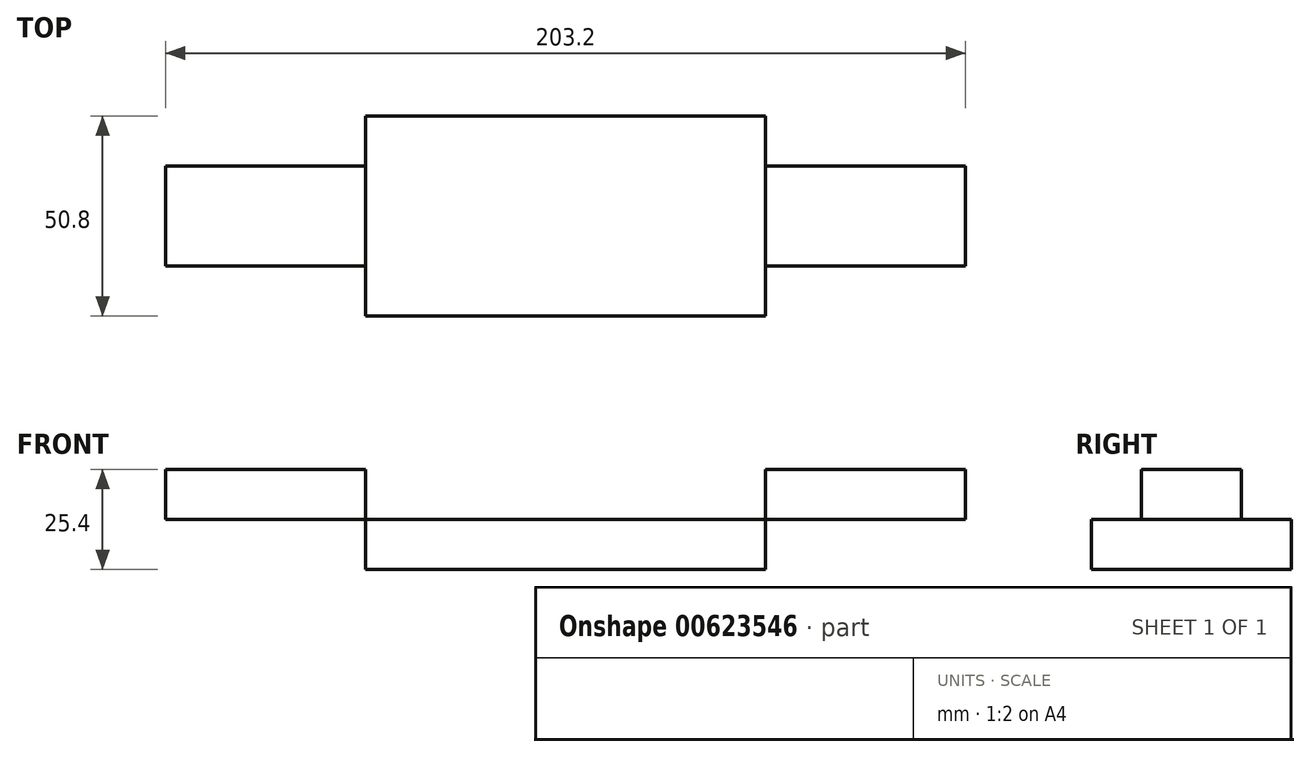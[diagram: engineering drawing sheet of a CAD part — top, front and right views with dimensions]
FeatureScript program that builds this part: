
annotation { "Feature Type Name" : "Feature", "Feature Type Description" : "" }
export const myFeature = defineFeature(function(context is Context, id is Id, definition is map)
    precondition{}
    {
        {
            var Q0;
            Q0=qCreatedBy(makeId("Top.planeOp"),FACE);
            var sketch = newSketch(context, id + "F0", { "sketchPlane" : qUnion([Q0])});
            skLineSegment(sketch, "E0.bottom", {"start": v(50.8, -25.4) * mm, "end": v(-50.8, -25.4) * mm});
            skLineSegment(sketch, "E0.top", {"start": v(50.8, 25.4) * mm, "end": v(-50.8, 25.4) * mm});
            skLineSegment(sketch, "E0.left", {"start": v(50.8, -25.4) * mm, "end": v(50.8, 25.4) * mm});
            skLineSegment(sketch, "E0.right", {"start": v(-50.8, -25.4) * mm, "end": v(-50.8, 25.4) * mm});
            skPoint(sketch, "E0.middle", {"position": v(0, 0) * mm});
            skSolve(sketch);
        }
        {
            var Q0;
            Q0 = qSketchRegion(id + "F0", true);
            extrude(context, id + "F1", {"entities" : qUnion([Q0]), "depth" : 12.7 * mm, "offsetDistance" : 25.4 * mm});
        }
        {
            var Q0;
            Q0=makeQuery(id+"F1.opExtrude","CAP_FACE",FACE,{"disambiguationData":[OSD([sQuery(id+"F0.wireOp",EDGE,"E0.bottom"),sQuery(id+"F0.wireOp",EDGE,"E0.top"),sQuery(id+"F0.wireOp",EDGE,"E0.left"),sQuery(id+"F0.wireOp",EDGE,"E0.right")])],"isStart":false});
            var sketch = newSketch(context, id + "F2", { "sketchPlane" : qUnion([Q0])});
            skLineSegment(sketch, "E1.bottom", {"start": v(101.6, -12.7) * mm, "end": v(0, -12.7) * mm});
            skLineSegment(sketch, "E1.top", {"start": v(101.6, 12.7) * mm, "end": v(0, 12.7) * mm});
            skLineSegment(sketch, "E1.left", {"start": v(101.6, -12.7) * mm, "end": v(101.6, 12.7) * mm});
            skPoint(sketch, "E1.middle", {"position": v(50.8, 0) * mm});
            skLineSegment(sketch, "E2.bottom", {"start": v(0, -12.7) * mm, "end": v(-101.6, -12.7) * mm});
            skLineSegment(sketch, "E2.top", {"start": v(0, 12.7) * mm, "end": v(-101.6, 12.7) * mm});
            skLineSegment(sketch, "E2.right", {"start": v(-101.6, -12.7) * mm, "end": v(-101.6, 12.7) * mm});
            skPoint(sketch, "E2.middle", {"position": v(-50.8, 0) * mm});
            skLineSegment(sketch, "E3", {"start": v(-50.8, 12.7) * mm, "end": v(-50.8, -12.7) * mm});
            skLineSegment(sketch, "E4", {"start": v(50.8, 12.7) * mm, "end": v(50.8, -12.7) * mm});
            skSolve(sketch);
        }
        {
            var Q0;
            {var subQ0=sQuery(id+"F2.wireOp",EDGE,"E1.left");Q0=makeQuery(id+"F2.imprint","IMPRINT",FACE,{"disambiguationData":[TD([[makeQuery(id+"F2.imprint","IMPRINT",EDGE,{"derivedFrom":subQ0}),1.0]])]});}
            var Q1;
            {var subQ0=sQuery(id+"F2.wireOp",EDGE,"E2.right");Q1=makeQuery(id+"F2.imprint","IMPRINT",FACE,{"disambiguationData":[TD([[makeQuery(id+"F2.imprint","IMPRINT",EDGE,{"derivedFrom":subQ0}),-1.0]])]});}
            extrude(context, id + "F3", {"entities" : qUnion([Q0, Q1]), "depth" : 12.7 * mm, "offsetDistance" : 25.4 * mm});
        }
    });
